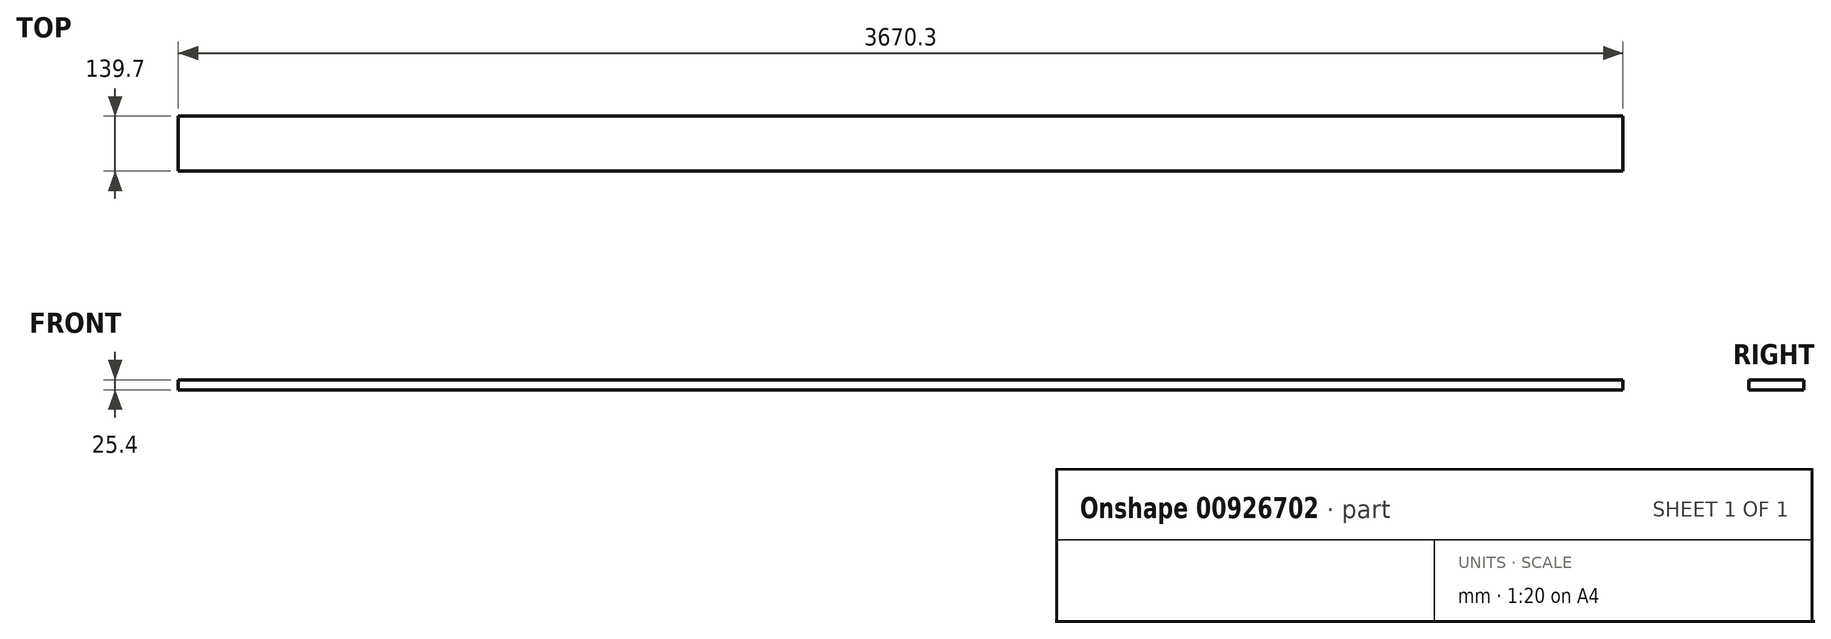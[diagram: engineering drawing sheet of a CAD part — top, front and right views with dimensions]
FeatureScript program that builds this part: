
annotation { "Feature Type Name" : "Feature", "Feature Type Description" : "" }
export const myFeature = defineFeature(function(context is Context, id is Id, definition is map)
    precondition{}
    {
        {
            var Q0;
            Q0=qCreatedBy(makeId("Right.planeOp"),FACE);
            var sketch = newSketch(context, id + "F0", { "sketchPlane" : qUnion([Q0])});
            skLineSegment(sketch, "E0.bottom", {"start": v(69.85, 12.7) * mm, "end": v(-69.85, 12.7) * mm});
            skLineSegment(sketch, "E0.top", {"start": v(69.85, -12.7) * mm, "end": v(-69.85, -12.7) * mm});
            skLineSegment(sketch, "E0.left", {"start": v(69.85, 12.7) * mm, "end": v(69.85, -12.7) * mm});
            skLineSegment(sketch, "E0.right", {"start": v(-69.85, 12.7) * mm, "end": v(-69.85, -12.7) * mm});
            skPoint(sketch, "E0.middle", {"position": v(0, 0) * mm});
            skSolve(sketch);
        }
        {
            var Q0;
            Q0=makeQuery(id+"F0.imprint","IMPRINT",FACE,{"disambiguationData":[TD([[makeQuery(id+"F0.imprint","IMPRINT",EDGE,{"derivedFrom":sQuery(id+"F0.wireOp",EDGE,"E0.bottom")}),1.0]])]});
            extrude(context, id + "F1", {"entities" : qUnion([Q0]), "depth" : 3670.3 * mm, "offsetDistance" : 25.4 * mm});
        }
    });
